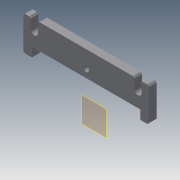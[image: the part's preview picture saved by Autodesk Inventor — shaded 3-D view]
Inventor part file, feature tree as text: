
AUTODESK INVENTOR PART (.ipt)
format: ipt  version: 2014 SP1 (Build 180222100, 222)  size: 117,760 bytes
history: native  units: in
note: dims shown in document units (in); Inventor stores cm internally (conversion verified against a paired STEP export)
features: plane x1, extrude x1, chamfer x1, sketch x1
ambient origin geometry x8: Origin, YZ Plane, XZ Plane, XY Plane, X Axis, Y Axis, Z Axis, Center Point
bodies: Solid1 (feature_tree)
feature tree (4):
  plane  "Work Plane1"
  extrude  "Extrusion1"  Depth=0.125in
  chamfer  "Chamfer1"  Distance=1.5in
  sketch  "Sketch1"  dims[d0=5.5in d1=2.75in d2=1.25in d3=1.5in d4=0.3409in d5=0.0in d6=0.325in d9=1.025in d10=0.475in d12=0.4in d15=4.75in d16=1.5in d17=2.375in d18=2.75in d19=1.225in d20=1.225in d22=0.25in d23=2.275in d24=1.1in d25=0.0625in d26=0.125in d27=45.0deg]
